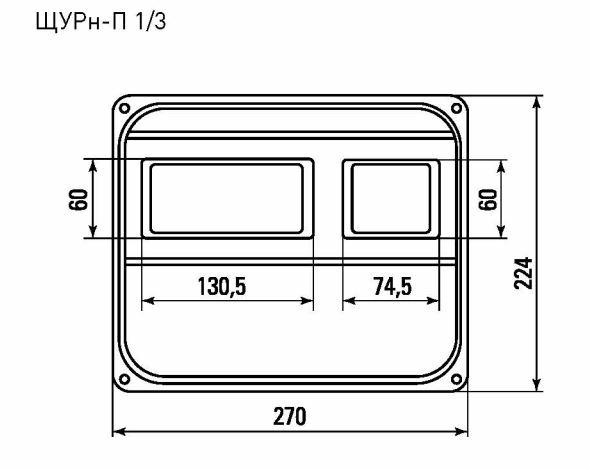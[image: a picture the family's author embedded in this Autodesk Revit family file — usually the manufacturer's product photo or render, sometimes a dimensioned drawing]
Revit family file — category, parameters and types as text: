
# Revit family: EKF_EE_Щит_Этажный_Слаботочный_Отсек_IP31_PROxima
name_source: partatom
category: Электрооборудование
units: mm (PartAtom-declared; Revit-internal decimal feet)

## family parameters
Всегда вертикально = Да
На основе рабочей плоскости = Нет
Общий = Нет
При загрузке вырезать с полостями = Нет
Размер круглого соединителя = Использовать диаметр
Тип детали = Силовой щит
Точка расчета площади = Да

## types (9) — shared parameters
ADSK_Единица измерения = компл.
ADSK_Завод-изготовитель = EKF
ADSK_Количество = 1
ADSK_Материал = RAL 7035_Сталь
ADSK_Размер_Высота = 1010 мм
ADSK_Размер_Глубина = 160 мм
ADSK_Размер_Ширина = 950 мм
Изготовитель = EKF
Серия номенклатуры = PROxima
Степень защиты IP = IP31
ТВ = EKF
Тип установки = Встраиваемый
zero-valued in all types: ADSK_Масса, Количество модулей на DIN-рейке

## per-type parameters (varying)
| type | ADSK_Код изделия | ADSK_Марка | ADSK_Наименование | ADSK_Обозначение | Количество DIN-реек | Максимальное количество модулей | Описание | Тип |
| ЩЭ 1 кв. (1010х950х160) IP31 EKF PROxima | mb10-v-1 | ЩЭ 1 кв. IP31 | Щит этажный ЩЭ 1 кв. (1010х950х160) IP31 EKF PROxima | ЩЭ 1 кв. IP31 | 5 | 18 | Щит этажный ЩЭ 1 кв. (1010х950х160) IP31 EKF PROxima | 157 мм |
| ЩЭ 8 кв. (1010х950х160) IP31 EKF PROxima | mb10-v-8 | ЩЭ 8 кв. IP31 | Щит этажный ЩЭ 8 кв. (1010х950х160) IP31 EKF PROxima | ЩЭ 8 кв. IP31 | 0 | 0 | Щит этажный ЩЭ 8 кв. (1010х950х160) IP31 EKF PROxima | 158 мм |
| ЩЭ 2 кв. (1010х950х160) IP31 EKF PROxima | mb10-v-2 | ЩЭ 2 кв. IP31 | Щит этажный ЩЭ 2 кв. (1010х950х160) IP31 EKF PROxima | ЩЭ 2 кв. IP31 | 5 | 18 | Щит этажный ЩЭ 2 кв. (1010х950х160) IP31 EKF PROxima | 159 мм |
| ЩЭ 3 кв. (1010х950х160) IP31 EKF PROxima | mb10-v-3 | ЩЭ 3 кв. IP31 | Щит этажный ЩЭ 3 кв. (1010х950х160) IP31 EKF PROxima | ЩЭ 3 кв. IP31 | 8 | 36 | Щит этажный ЩЭ 3 кв. (1010х950х160) IP31 EKF PROxima | 160 мм |
| ЩЭ 4 кв. (1010х950х160) IP31 EKF PROxima | mb10-v-4 | ЩЭ 4 кв. IP31 | Щит этажный ЩЭ 4 кв. (1010х950х160) IP31 EKF PROxima | ЩЭ 4 кв. IP31 | 8 | 36 | Щит этажный ЩЭ 4 кв. (1010х950х160) IP31 EKF PROxima | 161 мм |
| ЩЭ 4 кв. без окон (1010х950х160) IP31 EKF PROxima | mb10-v-4s | ЩЭ 4 кв. без окон IP31 | Щит этажный ЩЭ 4 кв. без окон (1010х950х160) IP31 EKF PROxima | ЩЭ 4 кв. без окон IP31 | 8 | 36 | Щит этажный ЩЭ 4 кв. без окон (1010х950х160) IP31 EKF PROxima | 162 мм |
| ЩЭ 5 кв. (1010х950х160) IP31 EKF PROxima | mb10-v-5 | ЩЭ 5 кв. IP31 | Щит этажный ЩЭ 5 кв. (1010х950х160) IP31 EKF PROxima | ЩЭ 5 кв. IP31 | 8 | 36 | Щит этажный ЩЭ 5 кв. (1010х950х160) IP31 EKF PROxima | 163 мм |
| ЩЭ 6 кв. (1010х950х160) IP31 EKF PROxima | mb10-v-6 | ЩЭ 6 кв. IP31 | Щит этажный ЩЭ 6 кв. (1010х950х160) IP31 EKF PROxima | ЩЭ 6 кв. IP31 | 8 | 36 | Щит этажный ЩЭ 6 кв. (1010х950х160) IP31 EKF PROxima | 164 мм |
| ЩЭ 7 кв. (1010х950х160) IP31 EKF PROxima | mb10-v-7 | ЩЭ 7 кв. IP31 | Щит этажный ЩЭ 7 кв. (1010х950х160) IP31 EKF PROxima | ЩЭ 7 кв. IP31 | 0 | 0 | Щит этажный ЩЭ 7 кв. (1010х950х160) IP31 EKF PROxima | 165 мм |
